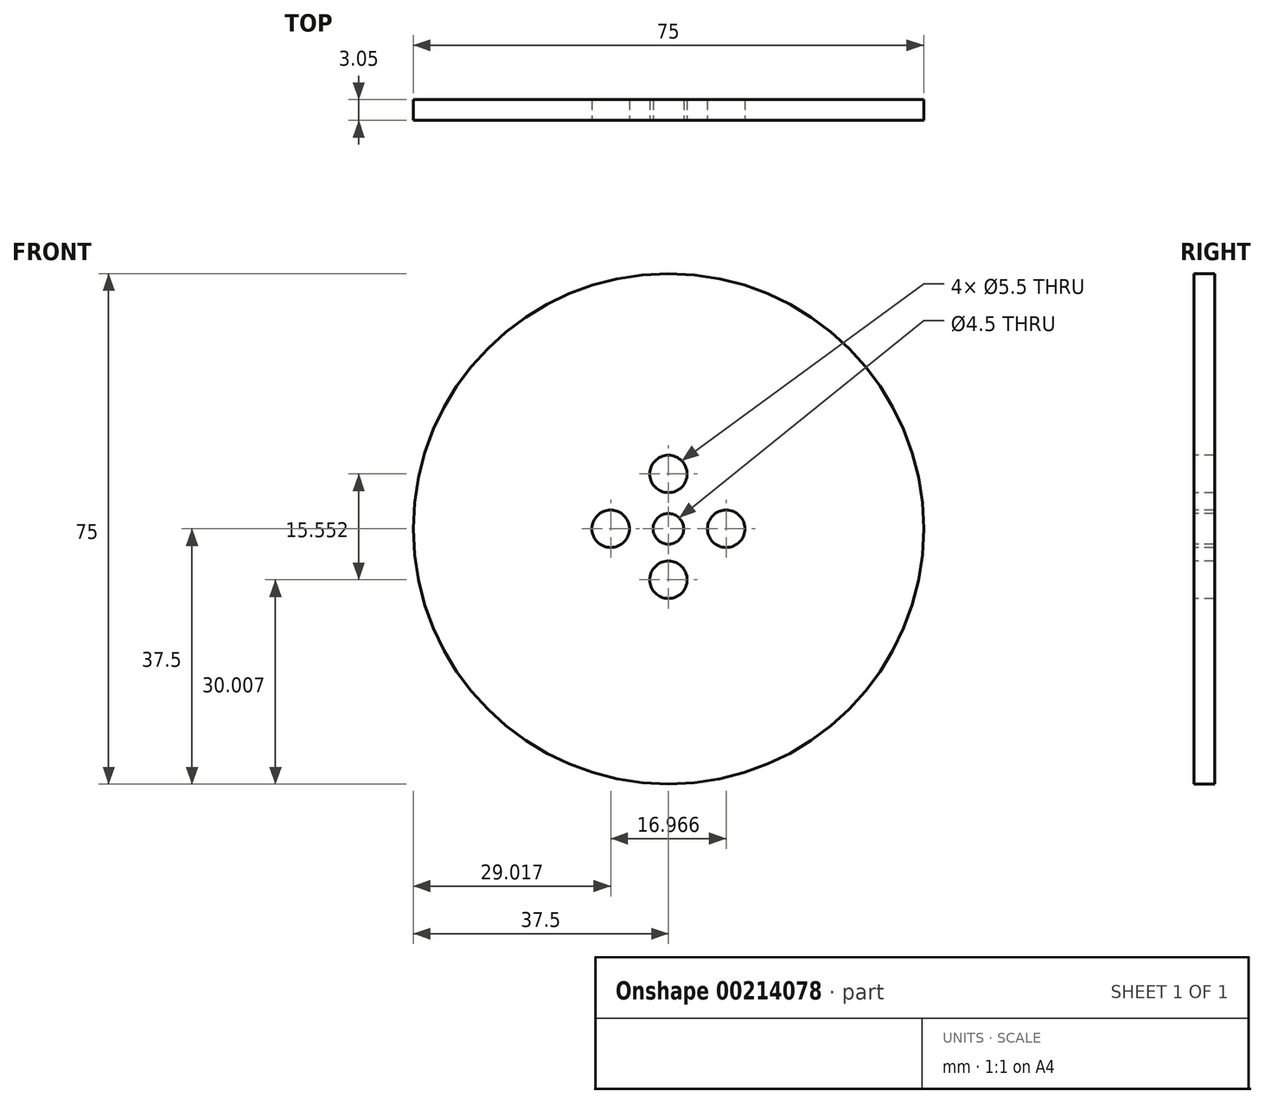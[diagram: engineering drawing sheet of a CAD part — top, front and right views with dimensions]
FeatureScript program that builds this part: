
annotation { "Feature Type Name" : "Feature", "Feature Type Description" : "" }
export const myFeature = defineFeature(function(context is Context, id is Id, definition is map)
    precondition{}
    {
        {
            var Q0;
            Q0=qCreatedBy(makeId("Front.planeOp"),FACE);
            var sketch = newSketch(context, id + "F0", { "sketchPlane" : qUnion([Q0])});
            skCircle(sketch, "E0", {"center": v(0, 0) * mm, "radius": 37.5 * mm});
            skSolve(sketch);
        }
        {
            var Q0;
            Q0=makeQuery(id+"F0.imprint","IMPRINT",FACE,{"disambiguationData":[TD([[makeQuery(id+"F0.imprint","IMPRINT",EDGE,{"derivedFrom":sQuery(id+"F0.wireOp",EDGE,"E0")}),1.0]])]});
            extrude(context, id + "F1", {"entities" : qUnion([Q0]), "depth" : 3.05 * mm});
        }
        {
            var Q0;
            Q0=sQuery(id+"F0.wireOp",VERTEX,"E0.center");
            var Q1;
            Q1=makeQuery(id+"F1.opExtrude","SWEPT_BODY",BODY,{"disambiguationData":[OSD([sQuery(id+"F0.wireOp",EDGE,"E0")])]});
            hole(context, id + "F2", {"style" : HoleStyle.SIMPLE, "endStyle" : HoleEndStyle.THROUGH, "oppositeDirection" : true, "holeDiameter" : 4.5 * mm, "locations" : qUnion([Q0]), "scope" : qUnion([Q1]), "isTappedThrough" : true, "startStyle" : HoleStartStyle.SKETCH});
        }
        {
            var Q0;
            Q0=qCreatedBy(makeId("Front.planeOp"),FACE);
            var sketch = newSketch(context, id + "F3", { "sketchPlane" : qUnion([Q0])});
            skPoint(sketch, "E1", {"position": v(0, 8.06) * mm});
            skPoint(sketch, "E2", {"position": v(8.48, 0) * mm});
            skPoint(sketch, "E3", {"position": v(0, -7.5) * mm});
            skPoint(sketch, "E4", {"position": v(-8.48, 0) * mm});
            skSolve(sketch);
        }
        {
            var Q0;
            Q0=sQuery(id+"F3.wireOp",VERTEX,"E1");
            var Q1;
            Q1=sQuery(id+"F3.wireOp",VERTEX,"E4");
            var Q2;
            Q2=sQuery(id+"F3.wireOp",VERTEX,"E3");
            var Q3;
            Q3=sQuery(id+"F3.wireOp",VERTEX,"E2");
            var Q4;
            Q4=makeQuery(id+"F1.opExtrude","SWEPT_BODY",BODY,{"disambiguationData":[OSD([sQuery(id+"F0.wireOp",EDGE,"E0")])]});
            hole(context, id + "F4", {"style" : HoleStyle.SIMPLE, "endStyle" : HoleEndStyle.THROUGH, "oppositeDirection" : true, "holeDiameter" : 5.5 * mm, "locations" : qUnion([Q0, Q1, Q2, Q3]), "scope" : qUnion([Q4]), "isTappedThrough" : true, "startStyle" : HoleStartStyle.SKETCH});
        }
    });
